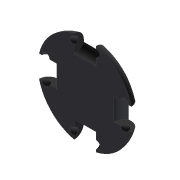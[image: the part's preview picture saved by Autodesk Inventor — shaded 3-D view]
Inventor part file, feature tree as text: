
AUTODESK INVENTOR PART (.ipt)
format: ipt  version: 2017 (Build 210142000, 142)  size: 147,456 bytes
history: native  units: mm
features: sketch x2, extrude x1, fillet x1, revolve x1, pattern_circular x1
ambient origin geometry x8: Origin, YZ Plane, XZ Plane, XY Plane, X Axis, Y Axis, Z Axis, Center Point
bodies: Solid1 (feature_tree)
feature tree (6):
  extrude  "Extrusion1"  Depth=6.0mm TaperAngle=0.0deg
  fillet  "Fillet1"  Radius=6.0mm
  revolve  "Revolution1"  [1 undecoded]
  pattern_circular  "Circular Pattern1"  [2 undecoded]
  sketch  "Sketch1"  dims[d0=60.0mm d1=6.0mm d2=0.0mm d3=6.0mm]
  sketch  "Sketch2"  dims[d4=14.0mm d5=7.0mm d6=18.0mm d7=5.0mm d8=5.0mm d9=90.0deg d10=40.0mm d11=360.0deg]
note: 3 required parameter values undecoded (feature->parameter linkage not recoverable at this tier; creation-order binding heuristic only, values carry confidence <= 0.55)